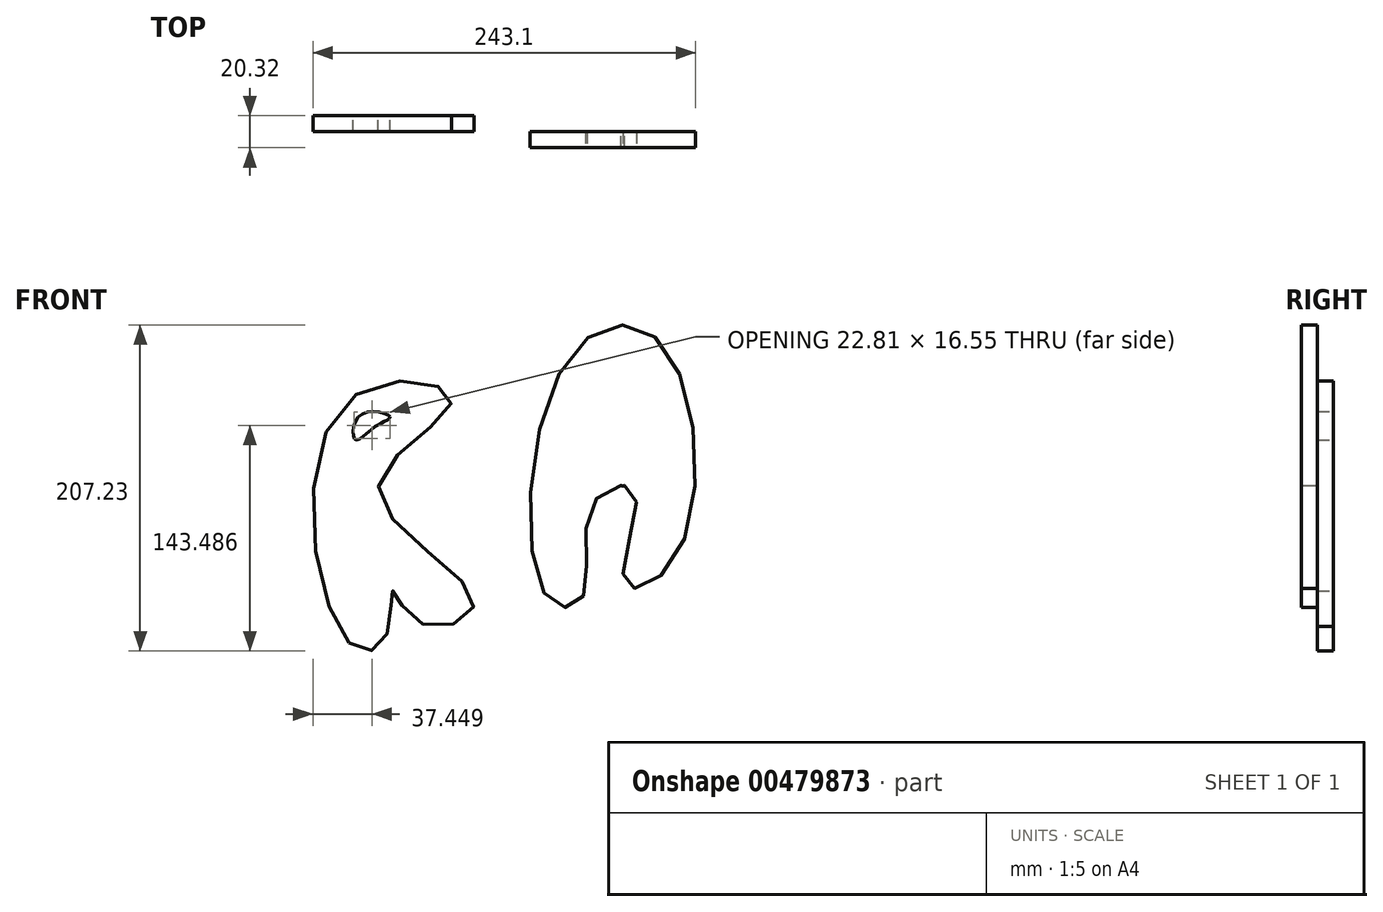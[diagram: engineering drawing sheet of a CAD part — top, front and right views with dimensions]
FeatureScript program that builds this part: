
annotation { "Feature Type Name" : "Feature", "Feature Type Description" : "" }
export const myFeature = defineFeature(function(context is Context, id is Id, definition is map)
    precondition{}
    {
        {
            var Q0;
            Q0=qCreatedBy(makeId("Front.planeOp"),FACE);
            var sketch = newSketch(context, id + "F0", { "sketchPlane" : qUnion([Q0])});
            skFitSpline(sketch, "E0", {"points": [v(-94.4, -82) * mm, v(-96.99, 70.28) * mm, v(-29.31, 72.15) * mm, v(-75.87, 15.6) * mm, v(-15.09, -56.08) * mm, v(-48.7, -69.67) * mm, v(-66.81, -49.03) * mm, v(-71.12, -78.73) * mm, v(-94.4, -82) * mm]});
            skFitSpline(sketch, "E1", {"points": [v(-68.54, 61.68) * mm, v(-77.16, 55.75) * mm, v(-90.52, 47.15) * mm, v(-87.07, 62.8) * mm, v(-68.54, 61.68) * mm]});
            skSolve(sketch);
        }
        {
            var Q0;
            Q0=makeQuery(id+"F0.imprint","IMPRINT",FACE,{"disambiguationData":[TD([[makeQuery(id+"F0.imprint","IMPRINT",EDGE,{"derivedFrom":sQuery(id+"F0.wireOp",EDGE,"E0")}),-1.0]])]});
            extrude(context, id + "F1", {"entities" : qUnion([Q0]), "depth" : 10.16 * mm});
        }
        {
            var Q0;
            Q0=makeQuery(id+"F1.opExtrude","CAP_FACE",FACE,{"disambiguationData":[OSD([sQuery(id+"F0.wireOp",EDGE,"E0"),sQuery(id+"F0.wireOp",EDGE,"E1")])],"isStart":false});
            var sketch = newSketch(context, id + "F2", { "sketchPlane" : qUnion([Q0])});
            skFitSpline(sketch, "E2", {"points": [v(32.33, -54.33) * mm, v(43.2, 96.23) * mm, v(102.17, 110.15) * mm, v(113.03, -27.93) * mm, v(80.44, -43.55) * mm, v(86.65, 14.11) * mm, v(60.27, 6.5) * mm, v(54.06, -52.71) * mm, v(32.33, -54.33) * mm]});
            skFitSpline(sketch, "E3", {"points": [v(63.37, 43.09) * mm, v(80.44, 46.7) * mm, v(80.44, 17.8) * mm, v(63.37, 43.09) * mm]});
            skSolve(sketch);
        }
        {
            var Q0;
            Q0 = qSketchRegion(id + "F2", true);
            extrude(context, id + "F3", {"entities" : qUnion([Q0]), "depth" : 10.16 * mm});
        }
    });
